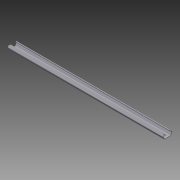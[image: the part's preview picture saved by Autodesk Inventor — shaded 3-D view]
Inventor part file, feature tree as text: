
AUTODESK INVENTOR PART (.ipt)
format: ipt  version: 2012 (Build 160160000, 160)  size: 522,752 bytes
history: native  units: in
note: dims shown in document units (in); Inventor stores cm internally (conversion verified against a paired STEP export)
features: sketch x3, extrude x2, other x1, imported_body x1
ambient origin geometry x8: Origin, YZ Plane, XZ Plane, XY Plane, X Axis, Y Axis, Z Axis, Center Point
feature tree (7):
  parser-record x1  (decoder bookkeeping rows leaked as tree rows — omitted from the tree; the rows remain in map.json)
  imported_body  "Base1"
  sketch  "Sketch1"  dims[d0=9.4488in d2=0.5in d3=0.3937in d5=1.0in d7=0.2in d8=0.0in]
  extrude  "Extrusion1"  Depth=0.2in TaperAngle=0.0deg
  extrude  "Extrusion2"  [1 undecoded]
  sketch  "Sketch2"  dims[d9=0.2in d10=0.0in]
  sketch  "Sketch3"
note: 1 required parameter value undecoded (feature->parameter linkage not recoverable at this tier; creation-order binding heuristic only, values carry confidence <= 0.55)
